FCSTD DOCUMENT  (FreeCAD 0.16R5692 (Git))
Label: thermaHousing
License: All rights reserved
LicenseURL: http://en.wikipedia.org/wiki/All_rights_reserved
objects: Sketcher::SketchObject×1
note: 1 computed .brp shape members not serialized (recipe doc carries the construction recipe); baked Part::Feature solids carry a one-line shape summary decoded from their .brp

FEATURE [Sketcher::SketchObject] Sketch
  sketch-geometry (10):
    g0: LineSegment StartX=-100 StartY=25 StartZ=0 EndX=100 EndY=25 EndZ=0
    g1: LineSegment StartX=100 StartY=25 StartZ=0 EndX=100 EndY=-25 EndZ=0
    g2: LineSegment StartX=100 StartY=-25 StartZ=0 EndX=-100 EndY=-25 EndZ=0
    g3: LineSegment StartX=-100 StartY=-25 StartZ=0 EndX=-100 EndY=25 EndZ=0
    g4: LineSegment StartX=-55 StartY=-1 StartZ=0 EndX=55 EndY=-1 EndZ=0
    g5: LineSegment StartX=55 StartY=-1 StartZ=0 EndX=55 EndY=1 EndZ=0
    g6: LineSegment StartX=55 StartY=1 StartZ=0 EndX=-55 EndY=1 EndZ=0
    g7: LineSegment StartX=-55 StartY=1 StartZ=0 EndX=-55 EndY=-1 EndZ=0
    g8: Circle CenterX=-60 CenterY=0 CenterZ=0 NormalX=0 NormalY=0 NormalZ=1 Radius=1.6
    g9: Circle CenterX=60 CenterY=0 CenterZ=0 NormalX=0 NormalY=0 NormalZ=1 Radius=1.6
  constraints (30):
    c: Coincident(g0,g1)
    c: Coincident(g1,g2)
    c: Coincident(g2,g3)
    c: Coincident(g3,g0)
    c: Horizontal(g0)
    c: Horizontal(g2)
    c: Vertical(g1)
    c: Vertical(g3)
    c: Symmetric(g0,g0,g-2)
    c: Symmetric(g0,g1,g-1)
    c: Coincident(g4,g5)
    c: Coincident(g5,g6)
    c: Coincident(g6,g7)
    c: Coincident(g7,g4)
    c: Horizontal(g4)
    c: Horizontal(g6)
    c: Vertical(g5)
    c: Vertical(g7)
    c: Symmetric(g6,g5,g-2)
    c: Symmetric(g5,g4,g-1)
    c: DistanceY(g5) = 2
    c: DistanceX(g6) = -110
    c: PointOnObject(g8,g-1)
    c: PointOnObject(g9,g-1)
    c: Equal(g9,g8)
    c: Symmetric(g9,g8,g-2)
    c: DistanceX(g-1,g8) = -60
    c: Radius(g8) = 1.6
    c: DistanceX(g0,g0) = 200
    c: DistanceY(g0,g2) = -50
